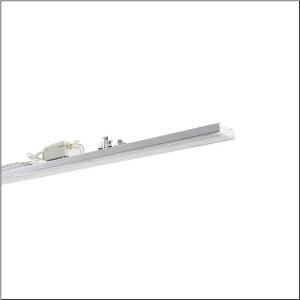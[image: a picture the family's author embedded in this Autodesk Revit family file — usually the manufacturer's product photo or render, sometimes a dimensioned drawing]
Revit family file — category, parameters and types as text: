
# Revit family: licross_11_recessed_mo_51te1emn495g
name_source: partatom
category: Lighting Fixtures
units: mm (PartAtom-declared; Revit-internal decimal feet)

## family parameters
Cut with Voids When Loaded = No
Host = Face
Light Source = No
Part Type = Normal
Room Calculation Point = No
Round Connector Dimension = Use Diameter
Shared = No

## types (1)
- --- (1 x LED, 9950 lm, 55.2 W, 4000K)
    Apparent Load = 55 VA
    CIE Flux Codes = 85 95 99 100 100
    Color Rendering = 80
    Color Temperature = 4000K
    Default Elevation = 1800 mm
    Description = Licross 11 Recessed MO, luminaire insert, of sheet steel, galvanised, coil coated, white, length: 1.500mm, width: 66mm, height: 67mm, LED rated luminous flux: 9.950lm, light colour: 840, SDCM (Standard Deviation of Colour Matching)MacAdam ≤ 2 SDCM (initial), control gear: ON/OFF Multilumen, with plug, 3-pole, with phase selection, mains connection: 220..240V, AC, 50/60Hz, rated input power: 55W, internal wiring halogen-free, primary light control with lens, of plastic, primary optical cover: cover, of PMMA, light emission: direct distribution, primary light characteristic: symmetric, protection rating (complete): IP54, insulation class (complete): insulation class I (protective earthing), certification: CE, ENEC, VDE, UKCA, protection symbol: D if used in an environment with non-conductive dust loads with corresponding accessories, impact resistance: IK06, permissible ambient temperature for indoor applications: -35..+40°C, corresponds to IFS (International Featured Standards) requirements for safety and quality in the food industry, reducing of maximum allowable ambient temperature of 5°C with ceiling mounting, The light source and the operating device comply with the requirements of the Ecodesign Regulation (EU) 2019/2020 and are replaceable in accordance with this regulation, packaging unit: 1 piece
    Height = 58 mm
    Lamp = 1 x LED
    Lamp Light Flux = 9950 lm
    Lamp Power = 55.2 W
    Lamp count = 1
    Length = 1500 mm
    Luminous efficacy = 180 lm/W
    Manufacturer = Siteco
    ModVariant = No
    Model = 51TE1EMN495G
    Mounting Place = Ceiling
    Mounting Type = Pendant
    Number of Poles = 1
    OnlyDefault = Yes
    Power Factor = 1
    Product Name = Licross 11 Recessed MO
    Product group = luminaire insert | ceiling pendant
    ProductGroupID = 901
    Protection Class = Protection class I
    Protection Degree = IP 54
    RLX_Detail_Level = 1
    RLX_Emergency_Light_Flux = 0 lm
    RLX_Emergency_Type = 0
    RLX_Emergency_Type_DB = No
    RlxData = <blob elided: 22649 chars, md5=32c3c1a4>
    Socket = socket
    Standby Power = 0 W
    System Light Flux = 9950 lm
    System Power = 55 W
    Type Comments = factory setting: luminous flux: 100 % | (A | C | E) | 126 mA
    Type Image = l_1296930.jpg
    URL = http://relux.com
    VarID = @adj_090813
    Voltage = 0 V
    Weight = 0.00 kg
    Width = 66 mm

## geometry (parser evidence)
native form markers: Blend x4, Sweep x12
no freeform markers — native parametric forms only
